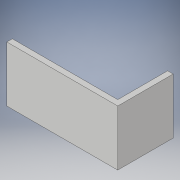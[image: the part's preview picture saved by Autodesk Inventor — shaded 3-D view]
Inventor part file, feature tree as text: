
AUTODESK INVENTOR PART (.ipt)
format: ipt  version: 2019 (Build 230136000, 136)  size: 114,688 bytes
history: native  units: in
note: dims shown in document units (in); Inventor stores cm internally (conversion verified against a paired STEP export)
features: extrude x3, sketch x3, other x1, shell x1
ambient origin geometry x8: Origin, YZ Plane, XZ Plane, XY Plane, X Axis, Y Axis, Z Axis, Center Point
bodies: Solid1 (feature_tree)
feature tree (8):
  other  "lift box"
  extrude  "Extrusion1"  Depth=3.0in
  shell  "Shell1"  Thickness=3.0in
  extrude  "Extrusion2"  Depth=0.3in
  extrude  "Extrusion3"  Depth=0.3in
  sketch  "Sketch1"  dims[d0=6.0in d1=3.0in d2=3.0in d3=0.0in]
  sketch  "Sketch2"  dims[d4=0.3in d5=0.3in]
  sketch  "Sketch3"  dims[d6=0.3in d7=0.3in d8=1.0in d9=0.0in d10=0.25in d11=0.5in d12=0.75in d13=1.0in d14=0.0in]
